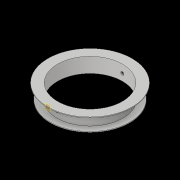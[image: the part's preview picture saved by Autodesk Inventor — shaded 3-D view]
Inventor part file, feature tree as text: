
AUTODESK INVENTOR PART (.ipt)
format: ipt  version: 2017 (Build 210142000, 142)  size: 121,344 bytes
history: native  units: in
note: dims shown in document units (in); Inventor stores cm internally (conversion verified against a paired STEP export)
features: sketch x2, revolve x1, plane x1, extrude x1
ambient origin geometry x8: Origin, YZ Plane, XZ Plane, XY Plane, X Axis, Y Axis, Z Axis, Center Point
bodies: Solid1 (feature_tree)
feature tree (5):
  revolve  "Revolution1"  [1 undecoded]
  plane  "Work Plane1"
  extrude  "Extrusion1"  Depth=0.125in
  sketch  "Sketch1"  dims[d0=2.0in d1=5.4375in]
  sketch  "Sketch2"  dims[d2=1.25in d3=0.125in d4=0.125in d5=2.25in d6=1.5in d7=0.125in d8=90.0deg d9=0.5in d10=1.0285in d11=1.0in d12=0.0in]
note: 1 required parameter value undecoded (feature->parameter linkage not recoverable at this tier; creation-order binding heuristic only, values carry confidence <= 0.55)
